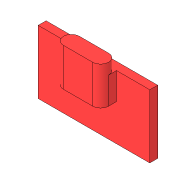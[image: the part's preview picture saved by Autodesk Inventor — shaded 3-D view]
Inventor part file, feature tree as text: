
AUTODESK INVENTOR PART (.ipt)
format: ipt  version: 2018.3 (Build 223284000, 284)  size: 104,448 bytes
history: native  units: in
note: dims shown in document units (in); Inventor stores cm internally (conversion verified against a paired STEP export)
features: extrude x2, sketch x2, fillet x1
ambient origin geometry x8: Origin, YZ Plane, XZ Plane, XY Plane, X Axis, Y Axis, Z Axis, Center Point
bodies: Solid1 (feature_tree)
feature tree (5):
  extrude  "Extrusion1"  Depth=0.5in
  extrude  "Extrusion2"  Depth=0.355in
  fillet  "Fillet1"  Radius=0.3in
  sketch  "Sketch1"  dims[d0=0.88in d1=0.5in]
  sketch  "Sketch2"  dims[d2=0.0625in d3=0.0in d8=0.355in d9=0.3in d10=0.2625in d11=0.125in d12=0.0in d13=0.0625in]
